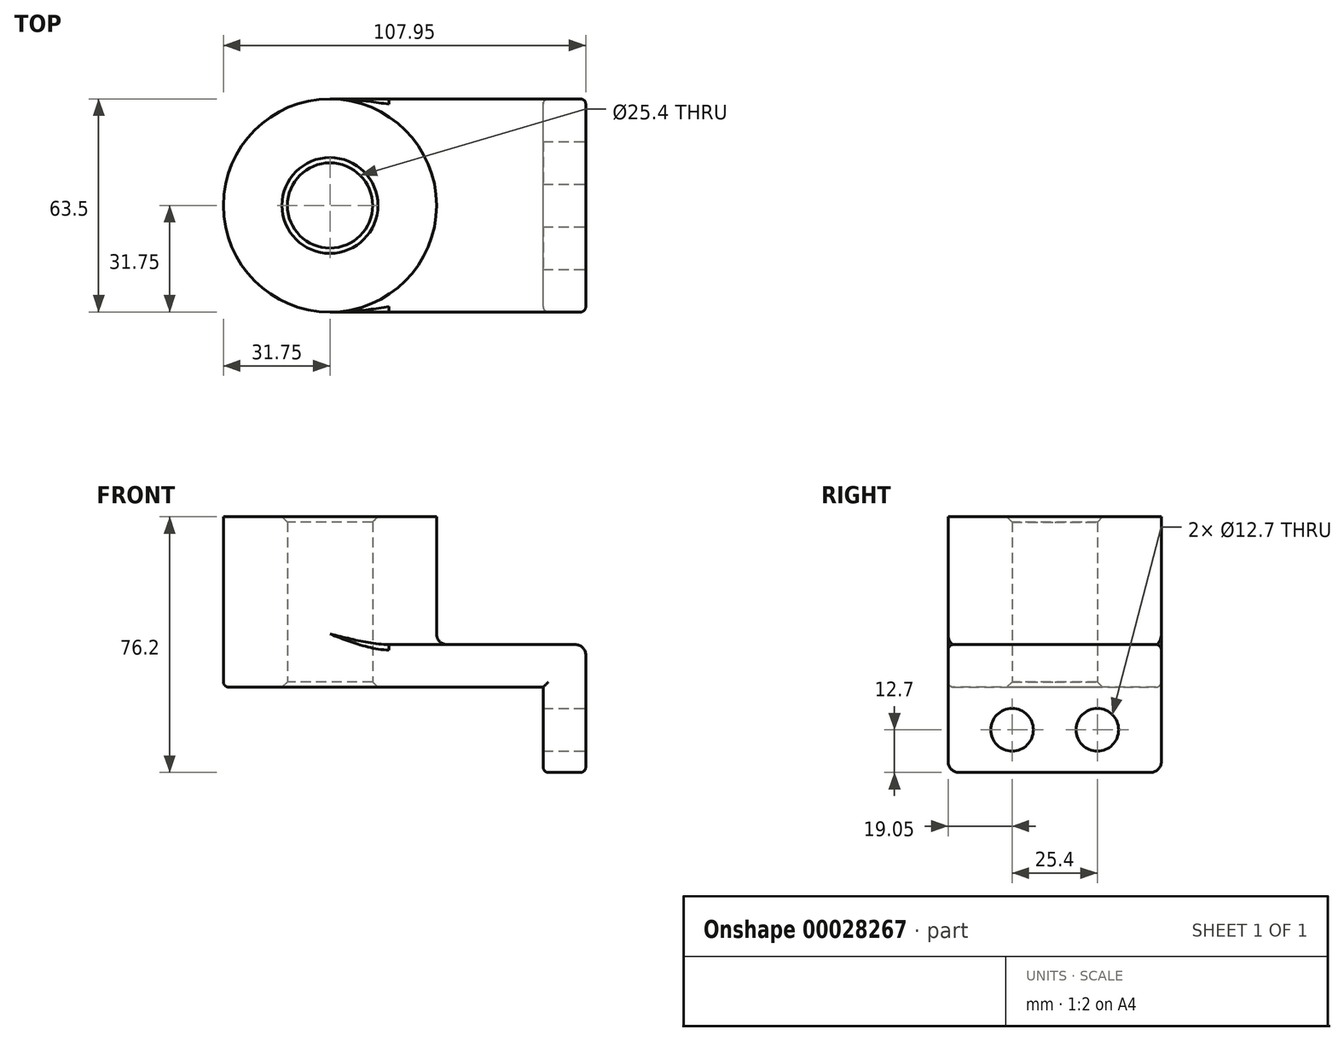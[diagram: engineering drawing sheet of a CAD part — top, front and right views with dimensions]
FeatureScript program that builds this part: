
annotation { "Feature Type Name" : "Feature", "Feature Type Description" : "" }
export const myFeature = defineFeature(function(context is Context, id is Id, definition is map)
    precondition{}
    {
        {
            var Q0;
            Q0=qCreatedBy(makeId("Top.planeOp"),FACE);
            var sketch = newSketch(context, id + "F0", { "sketchPlane" : qUnion([Q0])});
            skLineSegment(sketch, "E0.rect.bottom", {"start": v(38.1, 31.75) * mm, "end": v(-38.1, 31.75) * mm});
            skLineSegment(sketch, "E0.rect.top", {"start": v(38.1, -31.75) * mm, "end": v(-38.1, -31.75) * mm});
            skLineSegment(sketch, "E0.rect.left", {"start": v(38.1, 31.75) * mm, "end": v(38.1, -31.75) * mm});
            skLineSegment(sketch, "E0.rect.right", {"start": v(-38.1, 31.75) * mm, "end": v(-38.1, -31.75) * mm});
            skPoint(sketch, "E0.rect.middle", {"position": v(0, 0) * mm});
            skCircle(sketch, "E1", {"center": v(-38.1, 0) * mm, "radius": 31.75 * mm});
            skCircle(sketch, "E2", {"center": v(-38.1, 0) * mm, "radius": 12.7 * mm});
            skLineSegment(sketch, "E3", {"start": v(-69.85, 0) * mm, "end": v(38.1, 0) * mm, "construction": true});
            skSolve(sketch);
        }
        {
            var Q0;
            {var subQ1=sQuery(id+"F0.wireOp",EDGE,"E0.rect.right");Q0=makeQuery(id+"F0.imprint","IMPRINT",FACE,{"disambiguationData":[TD([[makeQuery(id+"F0.imprint","IMPRINT",EDGE,{"derivedFrom":subQ1}),-1.0]])]});}
            var Q1;
            {var subQ1=sQuery(id+"F0.wireOp",EDGE,"E0.rect.right");Q1=makeQuery(id+"F0.imprint","IMPRINT",FACE,{"disambiguationData":[TD([[makeQuery(id+"F0.imprint","IMPRINT",EDGE,{"derivedFrom":subQ1}),1.0]])]});}
            var Q2;
            {var subQ3=sQuery(id+"F0.wireOp",EDGE,"E0.rect.bottom");Q2=makeQuery(id+"F0.imprint","IMPRINT",FACE,{"disambiguationData":[TD([[makeQuery(id+"F0.imprint","IMPRINT",EDGE,{"derivedFrom":subQ3}),1.0]])]});}
            extrude(context, id + "F1", {"entities" : qUnion([Q0, Q1, Q2]), "depth" : 12.7 * mm});
        }
        {
            var Q0;
            {var subQ0=sQuery(id+"F0.wireOp",EDGE,"E2");var subQ1=sQuery(id+"F0.wireOp",EDGE,"E0.rect.right");var subQ3=makeQuery(id+"F0.imprint","INTERSECT",VERTEX,{"disambiguationData":[OD(0.0)],"derivedFrom":[subQ1,subQ0]});Q0=makeQuery(id+"F0.imprint","IMPRINT",FACE,{"disambiguationData":[TD([[makeQuery(id+"F0.imprint","IMPRINT",EDGE,{"disambiguationData":[TD([[subQ3,-1.0]])],"derivedFrom":subQ0}),-1.0]])]});}
            var Q1;
            {var subQ0=sQuery(id+"F0.wireOp",EDGE,"E2");var subQ1=sQuery(id+"F0.wireOp",EDGE,"E0.rect.right");var subQ3=makeQuery(id+"F0.imprint","INTERSECT",VERTEX,{"disambiguationData":[OD(0.0)],"derivedFrom":[subQ1,subQ0]});Q1=makeQuery(id+"F0.imprint","IMPRINT",FACE,{"disambiguationData":[TD([[makeQuery(id+"F0.imprint","IMPRINT",EDGE,{"disambiguationData":[TD([[subQ3,1.0]])],"derivedFrom":subQ0}),-1.0]])]});}
            extrude(context, id + "F2", {"entities" : qUnion([Q0, Q1]), "operationType" : NewBodyOperationType.ADD, "depth" : 50.8 * mm});
        }
        {
            var Q0;
            Q0=makeQuery(id+"F1.opExtrude","SWEPT_FACE",FACE,{"disambiguationData":[OSD([sQuery(id+"F0.wireOp",EDGE,"E0.rect.left")])]});
            var sketch = newSketch(context, id + "F3", { "sketchPlane" : qUnion([Q0])});
            skLineSegment(sketch, "E4.bottom", {"start": v(-31.75, 12.7) * mm, "end": v(31.75, 12.7) * mm});
            skLineSegment(sketch, "E4.top", {"start": v(-31.75, -25.4) * mm, "end": v(31.75, -25.4) * mm});
            skLineSegment(sketch, "E4.left", {"start": v(-31.75, 12.7) * mm, "end": v(-31.75, -25.4) * mm});
            skLineSegment(sketch, "E4.right", {"start": v(31.75, 12.7) * mm, "end": v(31.75, -25.4) * mm});
            skCircle(sketch, "E5", {"center": v(-12.7, -12.7) * mm, "radius": 6.35 * mm});
            skLineSegment(sketch, "E6", {"start": v(0, 12.7) * mm, "end": v(0, -25.4) * mm, "construction": true});
            skCircle(sketch, "E7.MirrorC", {"center": v(12.7, -12.7) * mm, "radius": 6.35 * mm});
            skSolve(sketch);
        }
        {
            var Q0;
            Q0 = qSketchRegion(id + "F3", true);
            extrude(context, id + "F4", {"entities" : qUnion([Q0]), "operationType" : NewBodyOperationType.ADD, "oppositeDirection" : true, "depth" : 12.7 * mm});
        }
        {
            var Q0;
            {var subQ0=sQuery(id+"F0.wireOp",EDGE,"E1");Q0=makeQuery(id+"F2.boolean.opBoolean","INTERSECT",EDGE,{"derivedFrom":[makeQuery(id+"F1.opExtrude","CAP_FACE",FACE,{"disambiguationData":[OSD([sQuery(id+"F0.wireOp",EDGE,"E0.rect.bottom"),sQuery(id+"F0.wireOp",EDGE,"E0.rect.top"),sQuery(id+"F0.wireOp",EDGE,"E0.rect.left"),subQ0,sQuery(id+"F0.wireOp",EDGE,"E2")])],"isStart":false}),makeQuery(id+"F2.opExtrude","SWEPT_FACE",FACE,{"disambiguationData":[OSD([subQ0])]})]});}
            var Q1;
            Q1=makeQuery(id+"F4.opExtrude","SWEPT_EDGE",EDGE,{"disambiguationData":[OSD([sQuery(id+"F3.wireOp",EDGE,"E4.top"),sQuery(id+"F3.wireOp",EDGE,"E4.left")])]});
            var Q2;
            Q2=makeQuery(id+"F4.opExtrude","SWEPT_EDGE",EDGE,{"disambiguationData":[OSD([sQuery(id+"F3.wireOp",EDGE,"E4.top"),sQuery(id+"F3.wireOp",EDGE,"E4.right")])]});
            var Q3;
            Q3=makeQuery(id+"F4.opExtrude","CAP_EDGE",EDGE,{"disambiguationData":[OSD([sQuery(id+"F3.wireOp",EDGE,"E4.bottom")])],"isStart":false});
            var Q4;
            Q4=makeQuery(id+"F1.opExtrude","CAP_EDGE",EDGE,{"disambiguationData":[OSD([sQuery(id+"F0.wireOp",EDGE,"E0.rect.left")])],"isStart":false});
            fillet(context, id + "F5", {"entities" : qUnion([Q0, Q1, Q2, Q3, Q4]), "radius" : 3.17 * mm, "tangentPropagation" : true, "allowEdgeOverflow" : false});
        }
        {
            var Q0;
            Q0=makeQuery(id+"F1.opExtrude","CAP_EDGE",EDGE,{"disambiguationData":[OSD([sQuery(id+"F0.wireOp",EDGE,"E0.rect.top")])],"isStart":false});
            var Q1;
            Q1=makeQuery(id+"F1.opExtrude","CAP_EDGE",EDGE,{"disambiguationData":[OSD([sQuery(id+"F0.wireOp",EDGE,"E0.rect.top")])],"isStart":true});
            var Q2;
            Q2=makeQuery(id+"F4.opExtrude","CAP_EDGE",EDGE,{"disambiguationData":[OSD([sQuery(id+"F3.wireOp",EDGE,"E4.left")])],"isStart":false});
            fillet(context, id + "F6", {"entities" : qUnion([Q0, Q1, Q2]), "radius" : 1.59 * mm, "tangentPropagation" : true, "allowEdgeOverflow" : false});
        }
        {
            var Q0;
            {var subQ0=sQuery(id+"F0.wireOp",EDGE,"E2");Q0=makeQuery(id+"F2.boolean.opBoolean","MERGE",FACE,{"derivedFrom":[makeQuery(id+"F1.opExtrude","SWEPT_FACE",FACE,{"disambiguationData":[OSD([subQ0])]}),makeQuery(id+"F2.opExtrude","SWEPT_FACE",FACE,{"disambiguationData":[OSD([subQ0])]})]});}
            chamfer(context, id + "F7", {"entities" : qUnion([Q0]), "width" : 1.59 * mm, "tangentPropagation" : true});
        }
    });
